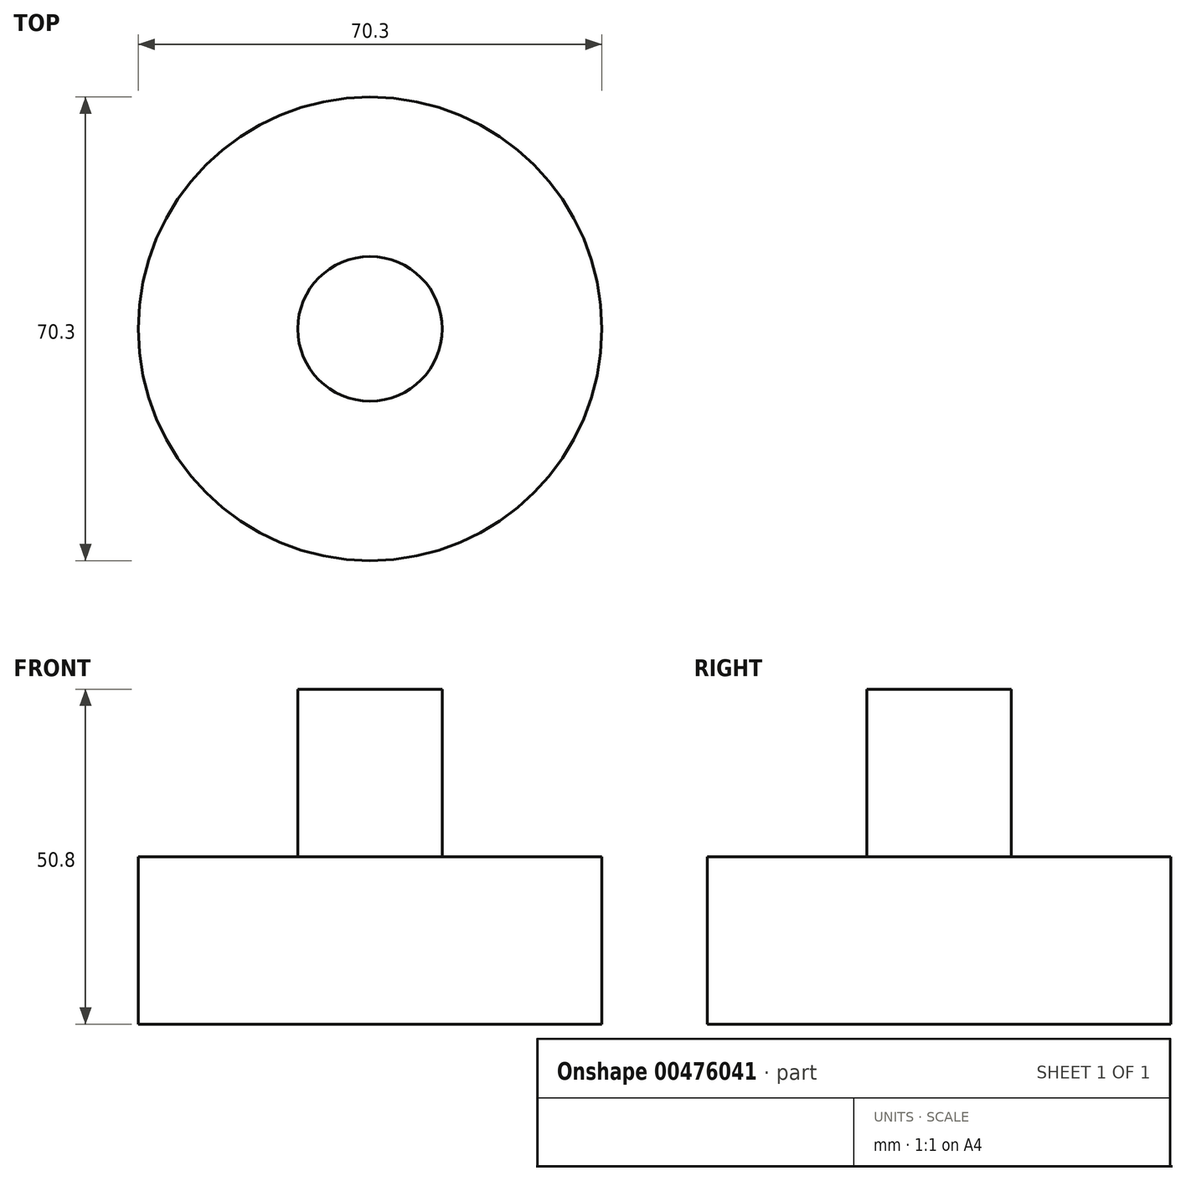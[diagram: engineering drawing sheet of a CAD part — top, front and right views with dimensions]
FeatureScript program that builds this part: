
annotation { "Feature Type Name" : "Feature", "Feature Type Description" : "" }
export const myFeature = defineFeature(function(context is Context, id is Id, definition is map)
    precondition{}
    {
        {
            var Q0;
            Q0=qCreatedBy(makeId("Top.planeOp"),FACE);
            var sketch = newSketch(context, id + "F0", { "sketchPlane" : qUnion([Q0])});
            skCircle(sketch, "E0", {"center": v(0, 0) * mm, "radius": 35.15 * mm});
            skSolve(sketch);
        }
        {
            var Q0;
            Q0 = qSketchRegion(id + "F0", true);
            extrude(context, id + "F1", {"entities" : qUnion([Q0]), "oppositeDirection" : true, "depth" : 25.4 * mm, "offsetDistance" : 25.4 * mm});
        }
        {
            var Q0;
            Q0=makeQuery(id+"F1.opExtrude","CAP_FACE",FACE,{"disambiguationData":[OSD([sQuery(id+"F0.wireOp",EDGE,"E0")])],"isStart":false});
            var sketch = newSketch(context, id + "F2", { "sketchPlane" : qUnion([Q0])});
            skCircle(sketch, "E1", {"center": v(0, 0) * mm, "radius": 10.96 * mm});
            skSolve(sketch);
        }
        {
            var Q0;
            Q0 = qSketchRegion(id + "F2", true);
            extrude(context, id + "F3", {"entities" : qUnion([Q0]), "operationType" : NewBodyOperationType.ADD, "oppositeDirection" : true, "depth" : 50.8 * mm, "offsetDistance" : 25.4 * mm});
        }
    });
